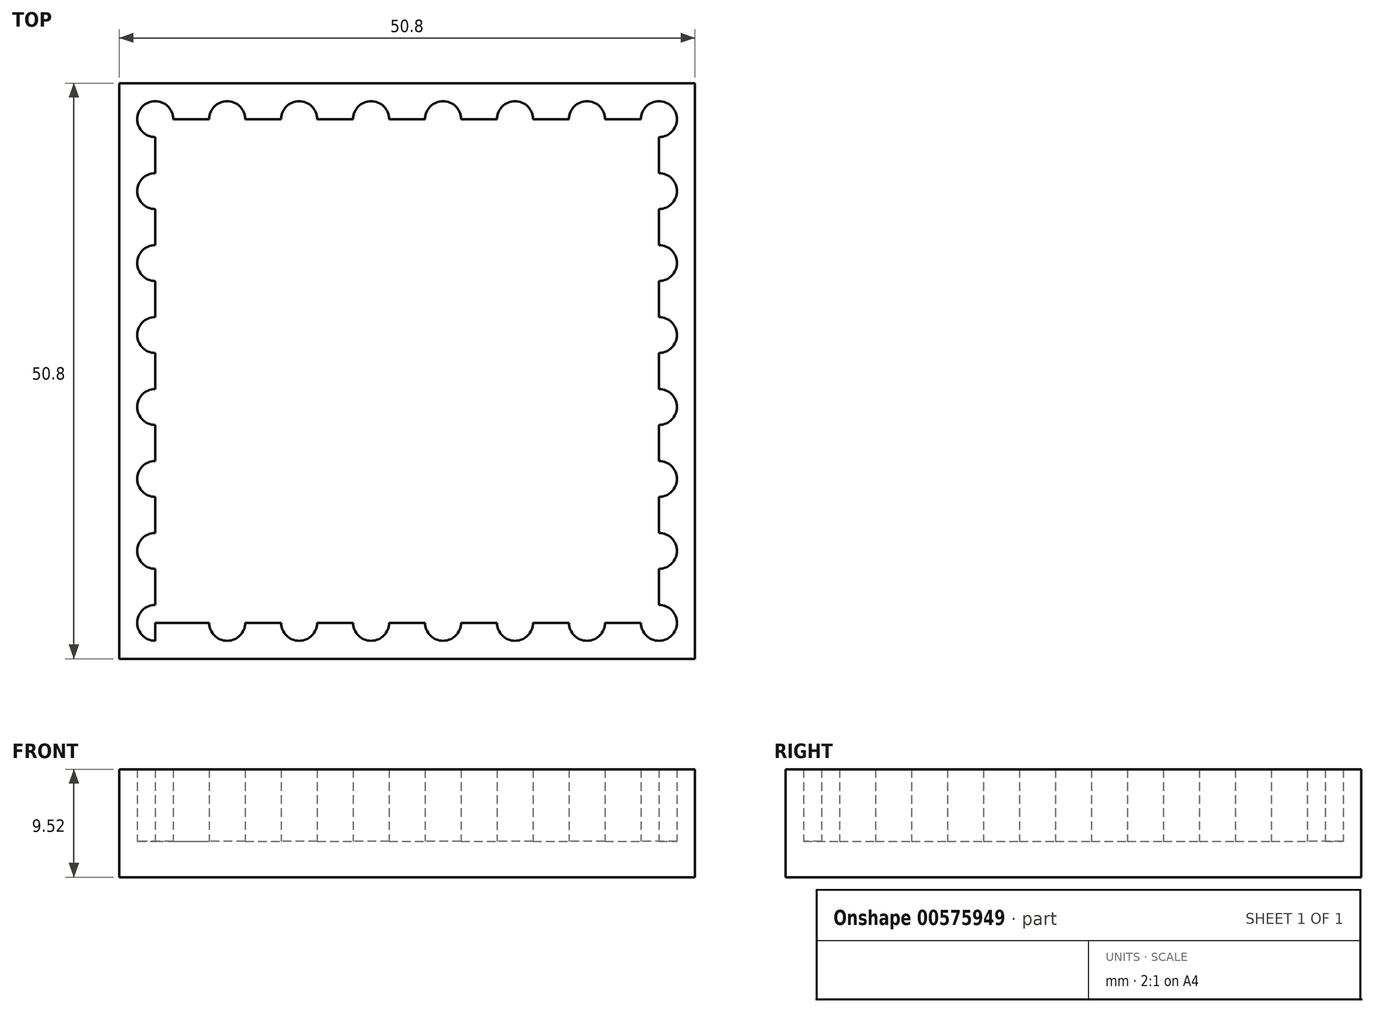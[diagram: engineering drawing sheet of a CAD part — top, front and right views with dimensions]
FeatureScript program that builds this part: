
annotation { "Feature Type Name" : "Feature", "Feature Type Description" : "" }
export const myFeature = defineFeature(function(context is Context, id is Id, definition is map)
    precondition{}
    {
        {
            var Q0;
            Q0=qCreatedBy(makeId("Top.planeOp"),FACE);
            var sketch = newSketch(context, id + "F0", { "sketchPlane" : qUnion([Q0])});
            skLineSegment(sketch, "E0.top", {"start": v(25.4, 25.4) * mm, "end": v(-25.4, 25.4) * mm});
            skLineSegment(sketch, "E0.left", {"start": v(25.4, -25.4) * mm, "end": v(25.4, 25.4) * mm});
            skLineSegment(sketch, "E0.right", {"start": v(-25.4, -25.4) * mm, "end": v(-25.4, 25.4) * mm});
            skPoint(sketch, "E0.middle", {"position": v(0, 0) * mm});
            skLineSegment(sketch, "E1", {"start": v(-25.4, 25.4) * mm, "end": v(-25.4, 22.23) * mm});
            skLineSegment(sketch, "E2", {"start": v(-25.4, 22.23) * mm, "end": v(-25.4, 15.87) * mm});
            skLineSegment(sketch, "E3", {"start": v(-25.4, 15.87) * mm, "end": v(-25.4, 9.52) * mm});
            skLineSegment(sketch, "E4", {"start": v(-25.4, -25.4) * mm, "end": v(-22.23, -25.4) * mm});
            skLineSegment(sketch, "E5", {"start": v(-25.4, 9.52) * mm, "end": v(-25.4, 3.17) * mm});
            skLineSegment(sketch, "E6", {"start": v(-25.4, 3.17) * mm, "end": v(-25.4, -3.18) * mm});
            skLineSegment(sketch, "E7", {"start": v(-25.4, -3.18) * mm, "end": v(-25.4, -9.53) * mm});
            skLineSegment(sketch, "E8", {"start": v(-25.4, -9.53) * mm, "end": v(-25.4, -15.87) * mm});
            skLineSegment(sketch, "E9", {"start": v(-25.4, -15.87) * mm, "end": v(-25.4, -25.4) * mm});
            skLineSegment(sketch, "E10", {"start": v(-22.23, -25.4) * mm, "end": v(-22.23, 25.4) * mm});
            skLineSegment(sketch, "E11", {"start": v(-25.4, 22.22) * mm, "end": v(25.4, 22.23) * mm});
            skCircle(sketch, "E12", {"center": v(-22.22, 22.22) * mm, "radius": 1.59 * mm});
            skLineSegment(sketch, "E13", {"start": v(-25.4, -25.4) * mm, "end": v(-25.4, -22.23) * mm});
            skLineSegment(sketch, "E14", {"start": v(-25.4, -22.23) * mm, "end": v(-25.4, -15.87) * mm});
            skLineSegment(sketch, "E15", {"start": v(-25.4, -22.23) * mm, "end": v(25.4, -22.23) * mm});
            skLineSegment(sketch, "E16", {"start": v(-25.4, -25.4) * mm, "end": v(25.4, -25.4) * mm});
            skLineSegment(sketch, "E17", {"start": v(-22.23, -25.4) * mm, "end": v(-15.88, -25.4) * mm});
            skLineSegment(sketch, "E18", {"start": v(-15.88, -25.4) * mm, "end": v(-9.52, -25.4) * mm});
            skLineSegment(sketch, "E19", {"start": v(-9.52, -25.4) * mm, "end": v(-3.17, -25.4) * mm});
            skLineSegment(sketch, "E20", {"start": v(-3.17, -25.4) * mm, "end": v(3.18, -25.4) * mm});
            skLineSegment(sketch, "E21", {"start": v(3.18, -25.4) * mm, "end": v(9.53, -25.4) * mm});
            skLineSegment(sketch, "E22", {"start": v(9.53, -25.4) * mm, "end": v(15.88, -25.4) * mm});
            skLineSegment(sketch, "E23", {"start": v(15.88, -25.4) * mm, "end": v(22.23, -25.4) * mm});
            skLineSegment(sketch, "E24", {"start": v(22.23, -25.4) * mm, "end": v(25.4, -25.4) * mm});
            skLineSegment(sketch, "E25", {"start": v(22.23, -25.4) * mm, "end": v(22.23, 25.4) * mm});
            skCircle(sketch, "E26", {"center": v(-22.23, -22.23) * mm, "radius": 1.59 * mm});
            skCircle(sketch, "E27", {"center": v(22.23, -22.23) * mm, "radius": 1.59 * mm});
            skCircle(sketch, "E28", {"center": v(22.23, 22.23) * mm, "radius": 1.59 * mm});
            skCircle(sketch, "E29.1.0.0", {"center": v(15.88, 22.23) * mm, "radius": 1.59 * mm});
            skCircle(sketch, "E29.2.0.0", {"center": v(9.53, 22.23) * mm, "radius": 1.59 * mm});
            skCircle(sketch, "E29.3.0.0", {"center": v(3.18, 22.23) * mm, "radius": 1.59 * mm});
            skCircle(sketch, "E29.4.0.0", {"center": v(-3.18, 22.23) * mm, "radius": 1.59 * mm});
            skCircle(sketch, "E29.5.0.0", {"center": v(-9.53, 22.23) * mm, "radius": 1.59 * mm});
            skCircle(sketch, "E29.6.0.0", {"center": v(-15.88, 22.23) * mm, "radius": 1.59 * mm});
            skLineSegment(sketch, "E29.direction1", {"start": v(22.23, 22.23) * mm, "end": v(15.88, 22.23) * mm, "construction": true});
            skCircle(sketch, "E30.1.0.0", {"center": v(-15.88, -22.23) * mm, "radius": 1.59 * mm});
            skCircle(sketch, "E30.2.0.0", {"center": v(-9.53, -22.23) * mm, "radius": 1.59 * mm});
            skCircle(sketch, "E30.3.0.0", {"center": v(-3.18, -22.23) * mm, "radius": 1.59 * mm});
            skCircle(sketch, "E30.4.0.0", {"center": v(3.17, -22.23) * mm, "radius": 1.59 * mm});
            skCircle(sketch, "E30.5.0.0", {"center": v(9.52, -22.23) * mm, "radius": 1.59 * mm});
            skCircle(sketch, "E30.6.0.0", {"center": v(15.87, -22.23) * mm, "radius": 1.59 * mm});
            skLineSegment(sketch, "E30.direction1", {"start": v(-22.23, -22.23) * mm, "end": v(-15.88, -22.23) * mm, "construction": true});
            skCircle(sketch, "E31.0.1.0", {"center": v(22.23, -15.88) * mm, "radius": 1.59 * mm});
            skCircle(sketch, "E31.0.2.0", {"center": v(22.23, -9.53) * mm, "radius": 1.59 * mm});
            skCircle(sketch, "E31.0.3.0", {"center": v(22.23, -3.18) * mm, "radius": 1.59 * mm});
            skCircle(sketch, "E31.0.4.0", {"center": v(22.23, 3.18) * mm, "radius": 1.59 * mm});
            skCircle(sketch, "E31.0.5.0", {"center": v(22.23, 9.53) * mm, "radius": 1.59 * mm});
            skCircle(sketch, "E31.0.6.0", {"center": v(22.23, 15.88) * mm, "radius": 1.59 * mm});
            skLineSegment(sketch, "E31.direction1", {"start": v(22.23, -22.23) * mm, "end": v(47.62, -22.23) * mm, "construction": true});
            skLineSegment(sketch, "E31.direction2", {"start": v(22.23, -22.23) * mm, "end": v(22.23, -15.88) * mm, "construction": true});
            skCircle(sketch, "E32.0.1.0", {"center": v(-22.23, -15.88) * mm, "radius": 1.59 * mm});
            skCircle(sketch, "E32.0.2.0", {"center": v(-22.23, -9.53) * mm, "radius": 1.59 * mm});
            skCircle(sketch, "E32.0.3.0", {"center": v(-22.23, -3.18) * mm, "radius": 1.59 * mm});
            skCircle(sketch, "E32.0.4.0", {"center": v(-22.23, 3.18) * mm, "radius": 1.59 * mm});
            skCircle(sketch, "E32.0.5.0", {"center": v(-22.23, 9.53) * mm, "radius": 1.59 * mm});
            skCircle(sketch, "E32.0.6.0", {"center": v(-22.23, 15.88) * mm, "radius": 1.59 * mm});
            skLineSegment(sketch, "E32.direction1", {"start": v(-22.23, -22.23) * mm, "end": v(3.17, -22.23) * mm, "construction": true});
            skLineSegment(sketch, "E32.direction2", {"start": v(-22.23, -22.23) * mm, "end": v(-22.23, -15.88) * mm, "construction": true});
            skSolve(sketch);
        }
        {
            var Q0;
            Q0 = qSketchRegion(id + "F0", true);
            var Q1;
            {var subQ47=sQuery(id+"F0.wireOp",EDGE,"E10");var subQ56=sQuery(id+"F0.wireOp",EDGE,"E26");var subQ57=makeQuery(id+"F0.imprint","INTERSECT",VERTEX,{"disambiguationData":[OD(1.0)],"derivedFrom":[subQ47,subQ56]});Q1=makeQuery(id+"F0.imprint","IMPRINT",FACE,{"disambiguationData":[TD([[makeQuery(id+"F0.imprint","IMPRINT",EDGE,{"disambiguationData":[TD([[subQ57,-1.0]])],"derivedFrom":subQ47}),-1.0]])]});}
            extrude(context, id + "F1", {"entities" : qUnion([Q0, Q1]), "depth" : 6.35 * mm, "offsetDistance" : 25.4 * mm});
        }
        {
            var Q0;
            Q0=makeQuery(id+"F1.opExtrude","CAP_FACE",FACE,{"disambiguationData":[OSD([sQuery(id+"F0.wireOp",EDGE,"E0.top"),sQuery(id+"F0.wireOp",EDGE,"E0.left"),sQuery(id+"F0.wireOp",EDGE,"E1"),sQuery(id+"F0.wireOp",EDGE,"E2"),sQuery(id+"F0.wireOp",EDGE,"E3"),sQuery(id+"F0.wireOp",EDGE,"E5"),sQuery(id+"F0.wireOp",EDGE,"E6"),sQuery(id+"F0.wireOp",EDGE,"E7"),sQuery(id+"F0.wireOp",EDGE,"E8"),sQuery(id+"F0.wireOp",EDGE,"E12"),sQuery(id+"F0.wireOp",EDGE,"E13"),sQuery(id+"F0.wireOp",EDGE,"E14"),sQuery(id+"F0.wireOp",EDGE,"E16"),sQuery(id+"F0.wireOp",EDGE,"E17"),sQuery(id+"F0.wireOp",EDGE,"E18"),sQuery(id+"F0.wireOp",EDGE,"E19"),sQuery(id+"F0.wireOp",EDGE,"E20"),sQuery(id+"F0.wireOp",EDGE,"E21"),sQuery(id+"F0.wireOp",EDGE,"E22"),sQuery(id+"F0.wireOp",EDGE,"E23"),sQuery(id+"F0.wireOp",EDGE,"E24"),sQuery(id+"F0.wireOp",EDGE,"E26"),sQuery(id+"F0.wireOp",EDGE,"E27"),sQuery(id+"F0.wireOp",EDGE,"E28"),sQuery(id+"F0.wireOp",EDGE,"E29.1.0.0"),sQuery(id+"F0.wireOp",EDGE,"E29.2.0.0"),sQuery(id+"F0.wireOp",EDGE,"E29.3.0.0"),sQuery(id+"F0.wireOp",EDGE,"E29.4.0.0"),sQuery(id+"F0.wireOp",EDGE,"E29.5.0.0"),sQuery(id+"F0.wireOp",EDGE,"E29.6.0.0"),sQuery(id+"F0.wireOp",EDGE,"E30.1.0.0"),sQuery(id+"F0.wireOp",EDGE,"E30.2.0.0"),sQuery(id+"F0.wireOp",EDGE,"E30.3.0.0"),sQuery(id+"F0.wireOp",EDGE,"E30.4.0.0"),sQuery(id+"F0.wireOp",EDGE,"E30.5.0.0"),sQuery(id+"F0.wireOp",EDGE,"E30.6.0.0"),sQuery(id+"F0.wireOp",EDGE,"E31.0.1.0"),sQuery(id+"F0.wireOp",EDGE,"E31.0.2.0"),sQuery(id+"F0.wireOp",EDGE,"E31.0.3.0"),sQuery(id+"F0.wireOp",EDGE,"E31.0.4.0"),sQuery(id+"F0.wireOp",EDGE,"E31.0.5.0"),sQuery(id+"F0.wireOp",EDGE,"E31.0.6.0"),sQuery(id+"F0.wireOp",EDGE,"E32.0.1.0"),sQuery(id+"F0.wireOp",EDGE,"E32.0.2.0"),sQuery(id+"F0.wireOp",EDGE,"E32.0.3.0"),sQuery(id+"F0.wireOp",EDGE,"E32.0.4.0"),sQuery(id+"F0.wireOp",EDGE,"E32.0.5.0"),sQuery(id+"F0.wireOp",EDGE,"E32.0.6.0")])],"isStart":true});
            var sketch = newSketch(context, id + "F2", { "sketchPlane" : qUnion([Q0])});
            skLineSegment(sketch, "E33.bottom", {"start": v(25.4, -25.4) * mm, "end": v(-25.4, -25.4) * mm});
            skLineSegment(sketch, "E33.top", {"start": v(25.4, 25.4) * mm, "end": v(-25.4, 25.4) * mm});
            skLineSegment(sketch, "E33.left", {"start": v(25.4, -25.4) * mm, "end": v(25.4, 25.4) * mm});
            skLineSegment(sketch, "E33.right", {"start": v(-25.4, -25.4) * mm, "end": v(-25.4, 25.4) * mm});
            skPoint(sketch, "E33.middle", {"position": v(0, 0) * mm});
            skSolve(sketch);
        }
        {
            var Q0;
            Q0 = qSketchRegion(id + "F2", true);
            extrude(context, id + "F3", {"entities" : qUnion([Q0]), "operationType" : NewBodyOperationType.ADD, "depth" : 3.17 * mm, "offsetDistance" : 25.4 * mm});
        }
    });
